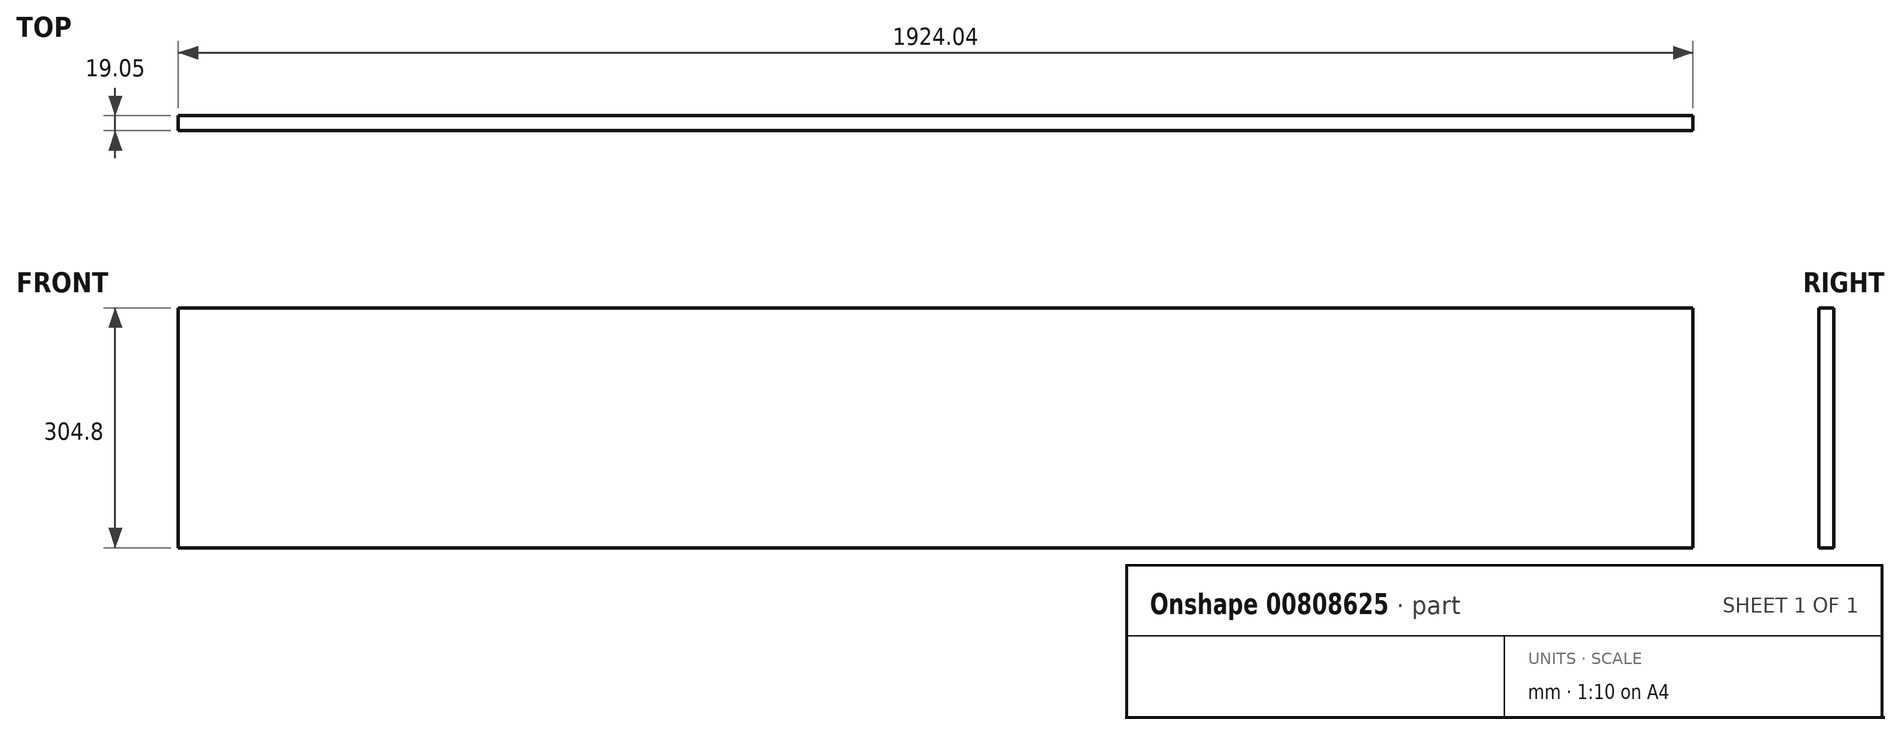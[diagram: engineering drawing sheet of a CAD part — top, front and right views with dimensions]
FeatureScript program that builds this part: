
annotation { "Feature Type Name" : "Feature", "Feature Type Description" : "" }
export const myFeature = defineFeature(function(context is Context, id is Id, definition is map)
    precondition{}
    {
        {
            var Q0;
            Q0=qCreatedBy(makeId("Front.planeOp"),FACE);
            var sketch = newSketch(context, id + "F0", { "sketchPlane" : qUnion([Q0])});
            skLineSegment(sketch, "E0.bottom", {"start": v(-962.03, 152.4) * mm, "end": v(962.02, 152.4) * mm});
            skLineSegment(sketch, "E0.top", {"start": v(-962.03, -152.4) * mm, "end": v(962.03, -152.4) * mm});
            skLineSegment(sketch, "E0.left", {"start": v(-962.03, 152.4) * mm, "end": v(-962.03, -152.4) * mm});
            skLineSegment(sketch, "E0.right", {"start": v(962.03, 152.4) * mm, "end": v(962.03, -152.4) * mm});
            skPoint(sketch, "E0.middle", {"position": v(0, 0) * mm});
            skSolve(sketch);
        }
        {
            var Q0;
            Q0=makeQuery(id+"F0.imprint","IMPRINT",FACE,{"disambiguationData":[TD([[makeQuery(id+"F0.imprint","IMPRINT",EDGE,{"derivedFrom":sQuery(id+"F0.wireOp",EDGE,"E0.bottom")}),-1.0]])]});
            extrude(context, id + "F1", {"entities" : qUnion([Q0]), "depth" : 19.05 * mm, "offsetDistance" : 25.4 * mm});
        }
    });
